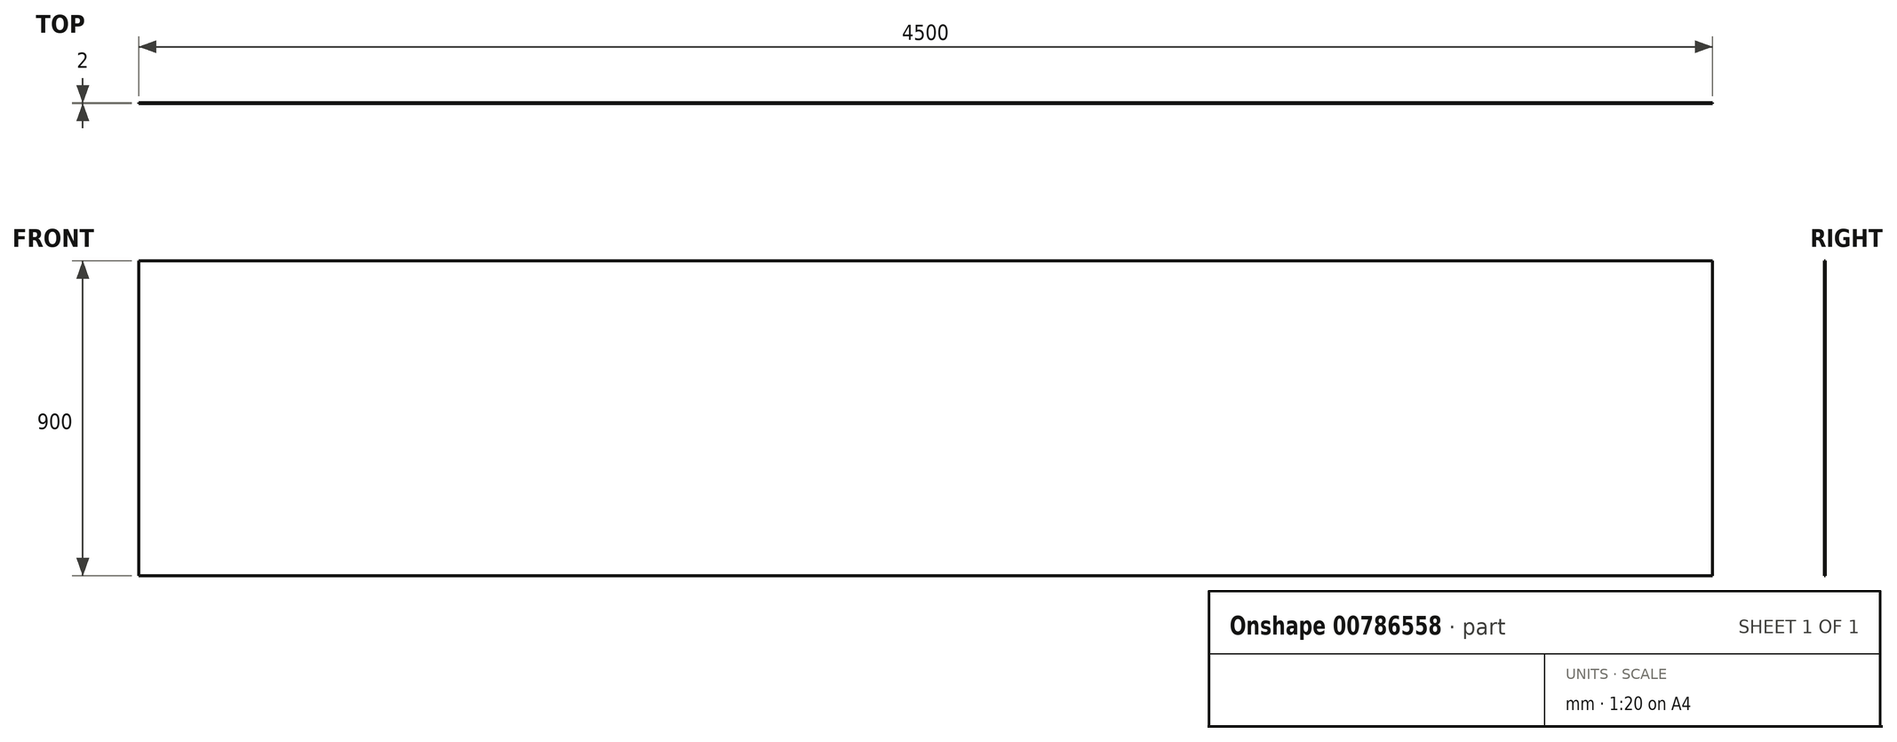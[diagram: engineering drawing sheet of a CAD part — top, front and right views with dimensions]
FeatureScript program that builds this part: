
annotation { "Feature Type Name" : "Feature", "Feature Type Description" : "" }
export const myFeature = defineFeature(function(context is Context, id is Id, definition is map)
    precondition{}
    {
        {
            var Q0;
            Q0=qCreatedBy(makeId("Front.planeOp"),FACE);
            var sketch = newSketch(context, id + "F0", { "sketchPlane" : qUnion([Q0])});
            skLineSegment(sketch, "E0.bottom", {"start": v(2250, 450) * mm, "end": v(-2250, 450) * mm});
            skLineSegment(sketch, "E0.top", {"start": v(2250, -450) * mm, "end": v(-2250, -450) * mm});
            skLineSegment(sketch, "E0.left", {"start": v(2250, 450) * mm, "end": v(2250, -450) * mm});
            skLineSegment(sketch, "E0.right", {"start": v(-2250, 450) * mm, "end": v(-2250, -450) * mm});
            skPoint(sketch, "E0.middle", {"position": v(0, 0) * mm});
            skSolve(sketch);
        }
        {
            var Q0;
            Q0=makeQuery(id+"F0.imprint","IMPRINT",FACE,{"disambiguationData":[TD([[makeQuery(id+"F0.imprint","IMPRINT",EDGE,{"derivedFrom":sQuery(id+"F0.wireOp",EDGE,"E0.bottom")}),1.0]])]});
            extrude(context, id + "F1", {"entities" : qUnion([Q0]), "depth" : 2 * mm, "offsetDistance" : 25 * mm});
        }
    });
